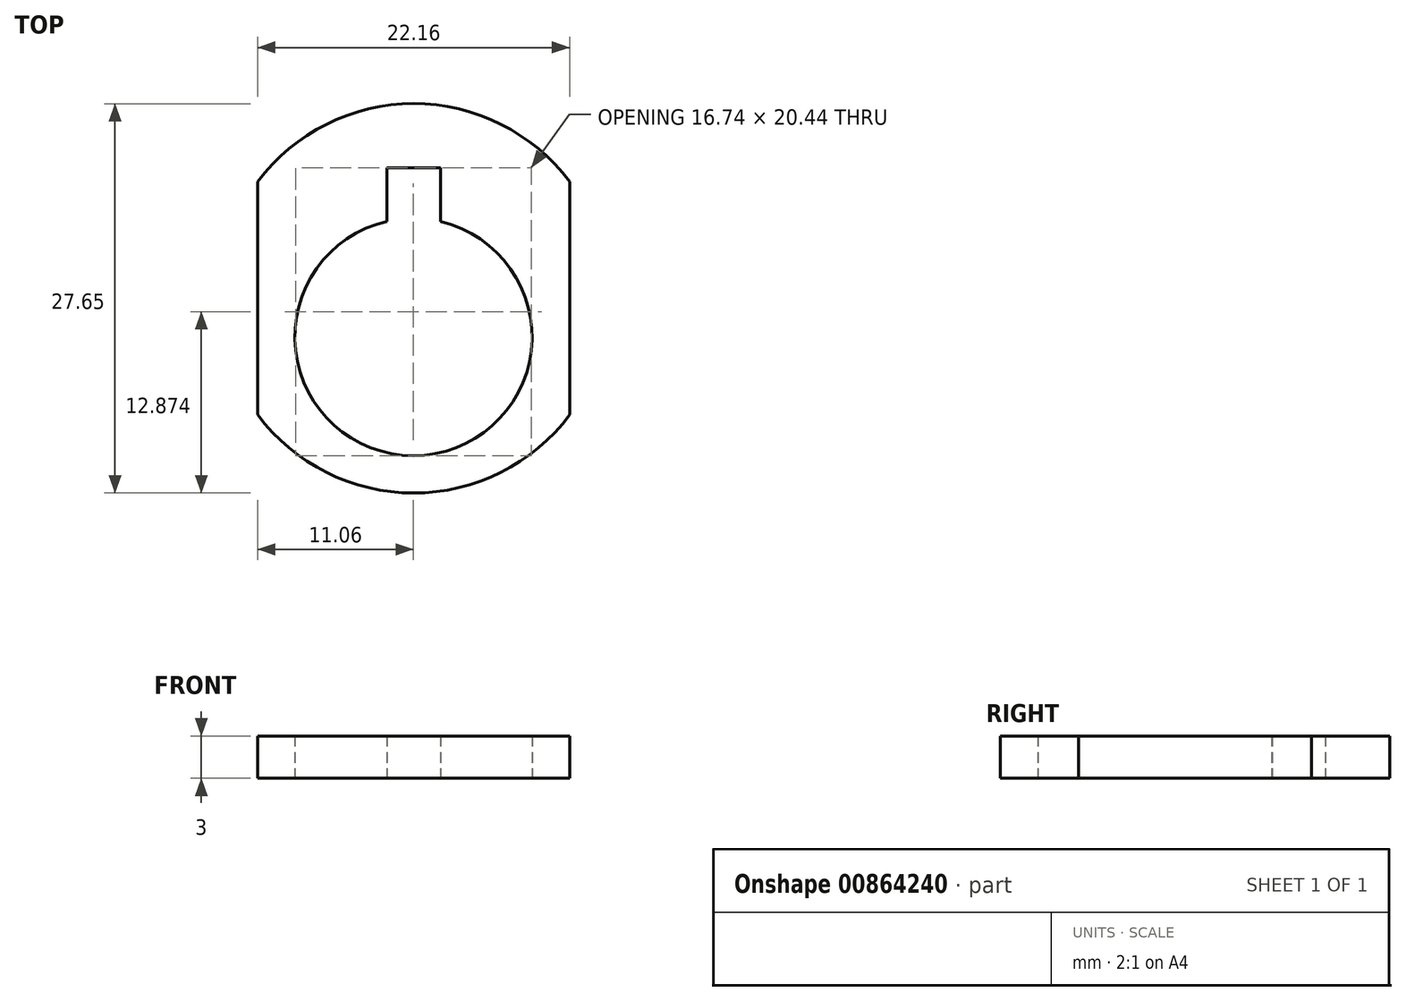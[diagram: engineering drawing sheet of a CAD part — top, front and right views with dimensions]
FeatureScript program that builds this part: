
annotation { "Feature Type Name" : "Feature", "Feature Type Description" : "" }
export const myFeature = defineFeature(function(context is Context, id is Id, definition is map)
    precondition{}
    {
        {
            var Q0;
            Q0=qCreatedBy(makeId("Top.planeOp"),FACE);
            var sketch = newSketch(context, id + "F0", { "sketchPlane" : qUnion([Q0])});
            skCircle(sketch, "E0", {"center": v(0, -2.75) * mm, "radius": 8.43 * mm});
            skSolve(sketch);
        }
        {
            var Q0;
            Q0=qCreatedBy(makeId("Top.planeOp"),FACE);
            var sketch = newSketch(context, id + "F1", { "sketchPlane" : qUnion([Q0])});
            skArc(sketch, "E1", {"start": v(-11.07, -8.27) * mm, "mid": v(0, -13.82) * mm, "end": v(11.08, -8.27) * mm});
            skLineSegment(sketch, "E2.right", {"start": v(-11.07, 8.27) * mm, "end": v(-11.07, -8.27) * mm});
            skLineSegment(sketch, "E3.right", {"start": v(11.07, 8.27) * mm, "end": v(11.08, -8.27) * mm});
            skArc(sketch, "E4.trimOffspring", {"start": v(11.07, 8.27) * mm, "mid": v(0, 13.83) * mm, "end": v(-11.08, 8.27) * mm});
            skArc(sketch, "E5", {"start": v(-1.9, 5.46) * mm, "mid": v(-0.04, -11.17) * mm, "end": v(1.9, 5.45) * mm});
            skLineSegment(sketch, "E6.top", {"start": v(1.9, 9.26) * mm, "end": v(-1.9, 9.26) * mm});
            skLineSegment(sketch, "E6.right", {"start": v(-1.9, 5.46) * mm, "end": v(-1.9, 9.26) * mm});
            skLineSegment(sketch, "E7", {"start": v(1.9, 9.26) * mm, "end": v(1.9, 5.45) * mm});
            skSolve(sketch);
        }
        {
            var Q0;
            Q0=makeQuery(id+"F1.imprint","IMPRINT",FACE,{"disambiguationData":[TD([[makeQuery(id+"F1.imprint","IMPRINT",EDGE,{"derivedFrom":sQuery(id+"F1.wireOp",EDGE,"E1")}),1.0]])]});
            extrude(context, id + "F2", {"entities" : qUnion([Q0]), "depth" : 3 * mm, "offsetDistance" : 25 * mm});
        }
    });
